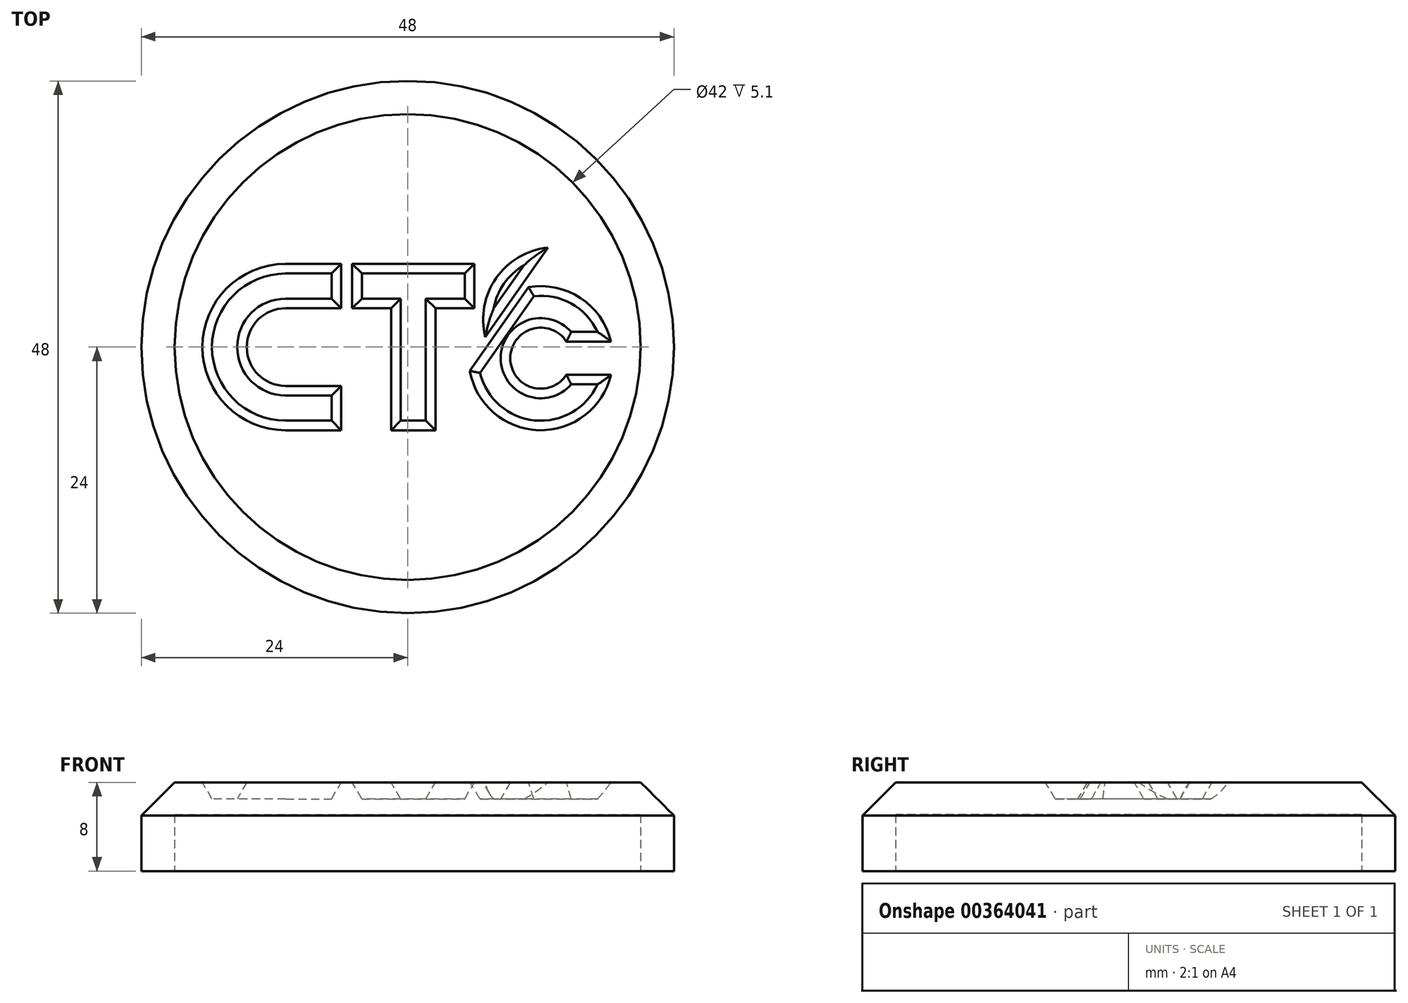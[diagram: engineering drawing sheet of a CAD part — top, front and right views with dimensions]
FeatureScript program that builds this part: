
annotation { "Feature Type Name" : "Feature", "Feature Type Description" : "" }
export const myFeature = defineFeature(function(context is Context, id is Id, definition is map)
    precondition{}
    {
        {
            var Q0;
            Q0=qCreatedBy(makeId("Top.planeOp"),FACE);
            var sketch = newSketch(context, id + "F0", { "sketchPlane" : qUnion([Q0])});
            skCircle(sketch, "E0", {"center": v(0, 0) * mm, "radius": 24 * mm});
            skSolve(sketch);
        }
        {
            var Q0;
            Q0 = qSketchRegion(id + "F0", true);
            extrude(context, id + "F1", {"entities" : qUnion([Q0]), "depth" : 8 * mm});
        }
        {
            var Q0;
            Q0=makeQuery(id+"F1.opExtrude","CAP_FACE",FACE,{"disambiguationData":[OSD([sQuery(id+"F0.wireOp",EDGE,"E0")])],"isStart":true});
            var sketch = newSketch(context, id + "F2", { "sketchPlane" : qUnion([Q0])});
            skCircle(sketch, "E1", {"center": v(0, 0) * mm, "radius": 21 * mm});
            skSolve(sketch);
        }
        {
            var Q0;
            Q0 = qSketchRegion(id + "F2", true);
            extrude(context, id + "F3", {"entities" : qUnion([Q0]), "operationType" : NewBodyOperationType.REMOVE, "oppositeDirection" : true, "depth" : 5.1 * mm});
        }
        {
            var Q0;
            Q0=makeQuery(id+"F1.opExtrude","CAP_EDGE",EDGE,{"disambiguationData":[OSD([sQuery(id+"F0.wireOp",EDGE,"E0")])],"isStart":false});
            chamfer(context, id + "F4", {"entities" : qUnion([Q0]), "width" : 3 * mm, "tangentPropagation" : true});
        }
        {
            var Q0;
            Q0=makeQuery(id+"F1.opExtrude","CAP_FACE",FACE,{"disambiguationData":[OSD([sQuery(id+"F0.wireOp",EDGE,"E0")])],"isStart":false});
            var sketch = newSketch(context, id + "F5", { "sketchPlane" : qUnion([Q0])});
            skLineSegment(sketch, "E2", {"start": v(0, 0) * mm, "end": v(0, -7.5) * mm, "construction": true});
            skLineSegment(sketch, "E3", {"start": v(0, -7.5) * mm, "end": v(-18, -7.5) * mm, "construction": true});
            skLineSegment(sketch, "E4", {"start": v(0, -7.5) * mm, "end": v(18, -7.5) * mm, "construction": true});
            skLineSegment(sketch, "E5", {"start": v(-11, -7.5) * mm, "end": v(-11, 7.5) * mm, "construction": true});
            skLineSegment(sketch, "E6", {"start": v(0.5, -7.5) * mm, "end": v(0.5, 7.5) * mm, "construction": true});
            skLineSegment(sketch, "E7", {"start": v(12, -7.5) * mm, "end": v(12, 5.5) * mm, "construction": true});
            skLineSegment(sketch, "E8", {"start": v(-11, 7.5) * mm, "end": v(-6, 7.5) * mm});
            skLineSegment(sketch, "E9", {"start": v(-6, 7.5) * mm, "end": v(-6, 3.5) * mm});
            skLineSegment(sketch, "E10", {"start": v(-6, 3.5) * mm, "end": v(-11, 3.5) * mm});
            skArc(sketch, "E11", {"start": v(-11, 3.5) * mm, "mid": v(-14.5, 0) * mm, "end": v(-11, -3.5) * mm});
            skLineSegment(sketch, "E12", {"start": v(-11, -7.5) * mm, "end": v(-6, -7.5) * mm});
            skLineSegment(sketch, "E13", {"start": v(-6, -7.5) * mm, "end": v(-6, -3.5) * mm});
            skLineSegment(sketch, "E14", {"start": v(-6, -3.5) * mm, "end": v(-11, -3.5) * mm});
            skArc(sketch, "E15", {"start": v(-11, 7.5) * mm, "mid": v(-18.5, 0) * mm, "end": v(-11, -7.5) * mm});
            skLineSegment(sketch, "E16", {"start": v(0.5, 7.5) * mm, "end": v(-5, 7.5) * mm});
            skLineSegment(sketch, "E17", {"start": v(-5, 7.5) * mm, "end": v(-5, 3.5) * mm});
            skLineSegment(sketch, "E18", {"start": v(-5, 3.5) * mm, "end": v(-1.5, 3.5) * mm});
            skLineSegment(sketch, "E19", {"start": v(-1.5, 3.5) * mm, "end": v(-1.5, -7.5) * mm});
            skLineSegment(sketch, "E20", {"start": v(-1.5, -7.5) * mm, "end": v(0.5, -7.5) * mm});
            skLineSegment(sketch, "E21", {"start": v(0.5, -7.5) * mm, "end": v(2.5, -7.5) * mm});
            skLineSegment(sketch, "E22", {"start": v(2.5, -7.5) * mm, "end": v(2.5, 3.5) * mm});
            skLineSegment(sketch, "E23", {"start": v(2.5, 3.5) * mm, "end": v(6, 3.5) * mm});
            skLineSegment(sketch, "E24", {"start": v(6, 3.5) * mm, "end": v(6, 7.5) * mm});
            skLineSegment(sketch, "E25", {"start": v(6, 7.5) * mm, "end": v(0.5, 7.5) * mm});
            skArc(sketch, "E26", {"start": v(18.32, 0.5) * mm, "mid": v(15.58, 4.43) * mm, "end": v(10.88, 5.4) * mm});
            skArc(sketch, "E27", {"start": v(14.3, 0.5) * mm, "mid": v(9.25, -1) * mm, "end": v(14.3, -2.5) * mm});
            skLineSegment(sketch, "E28", {"start": v(12, -1) * mm, "end": v(18.5, -1) * mm, "construction": true});
            skLineSegment(sketch, "E29.0", {"start": v(14.3, -2.5) * mm, "end": v(18.32, -2.5) * mm});
            skLineSegment(sketch, "E30.0", {"start": v(14.3, 0.5) * mm, "end": v(18.32, 0.5) * mm});
            skLineSegment(sketch, "E31", {"start": v(12, 5.5) * mm, "end": v(12, 7) * mm, "construction": true});
            skLineSegment(sketch, "E32", {"start": v(10.88, 5.4) * mm, "end": v(5.6, -2.14) * mm});
            skLineSegment(sketch, "E33", {"start": v(12, 2.5) * mm, "end": v(13.3, 2.5) * mm, "construction": true});
            skLineSegment(sketch, "E34.0", {"start": v(12.64, 8.97) * mm, "end": v(7, 0.9) * mm});
            skArc(sketch, "E35", {"start": v(12.64, 8.97) * mm, "mid": v(7.98, 6.23) * mm, "end": v(7, 0.9) * mm});
            skArc(sketch, "E36.trimOffspring", {"start": v(5.6, -2.14) * mm, "mid": v(11.82, -7.5) * mm, "end": v(18.32, -2.5) * mm});
            skSolve(sketch);
        }
        {
            var Q0;
            Q0 = qSketchRegion(id + "F5", true);
            extrude(context, id + "F6", {"entities" : qUnion([Q0]), "operationType" : NewBodyOperationType.REMOVE, "oppositeDirection" : true, "depth" : 1.5 * mm, "hasDraft" : true, "draftAngle" : 30 * degree, "draftPullDirection" : true});
        }
    });
